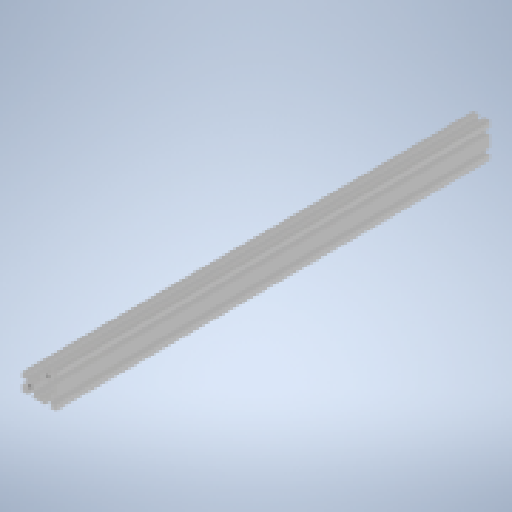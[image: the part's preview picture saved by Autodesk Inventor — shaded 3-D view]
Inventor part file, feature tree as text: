
AUTODESK INVENTOR PART (.ipt)
format: ipt  version: 2024 (Build 280153000, 153)  size: 442,368 bytes
history: native  units: mm
features: thread x4, sketch x3, hole x2, extrude x1
ambient origin geometry x8: Origin, YZ Plane, XZ Plane, XY Plane, X Axis, Y Axis, Z Axis, Center Point
bodies: Solid1 (feature_tree)
feature tree (10):
  extrude  "Extrusion1"  Depth=10.0mm TaperAngle=0.0deg
  hole  "Hole1"  [1 undecoded]
  hole  "Hole2"  [1 undecoded]
  thread  "Thread1"  [1 undecoded]
  thread  "Thread2"  [1 undecoded]
  thread  "Thread3"  [1 undecoded]
  thread  "Thread4"  [1 undecoded]
  sketch  "Sketch_1"  dims[d0=425.0mm d1=0.0mm]
  sketch  "Sketch2"  dims[d2=4.2mm d3=6.0mm d4=4.0mm d5=2.0mm d6=90.0deg d7=425.0mm d8=0.0mm]
  sketch  "Sketch3"  dims[d9=4.2mm d10=6.0mm d11=4.0mm d12=2.0mm d13=90.0deg d14=425.0mm d15=0.0mm d16=10.0mm d17=0.0mm d18=10.0mm d19=0.0mm d20=10.0mm d21=0.0mm d22=10.0mm d23=0.0mm]
note: 6 required parameter values undecoded (feature->parameter linkage not recoverable at this tier; creation-order binding heuristic only, values carry confidence <= 0.55)
